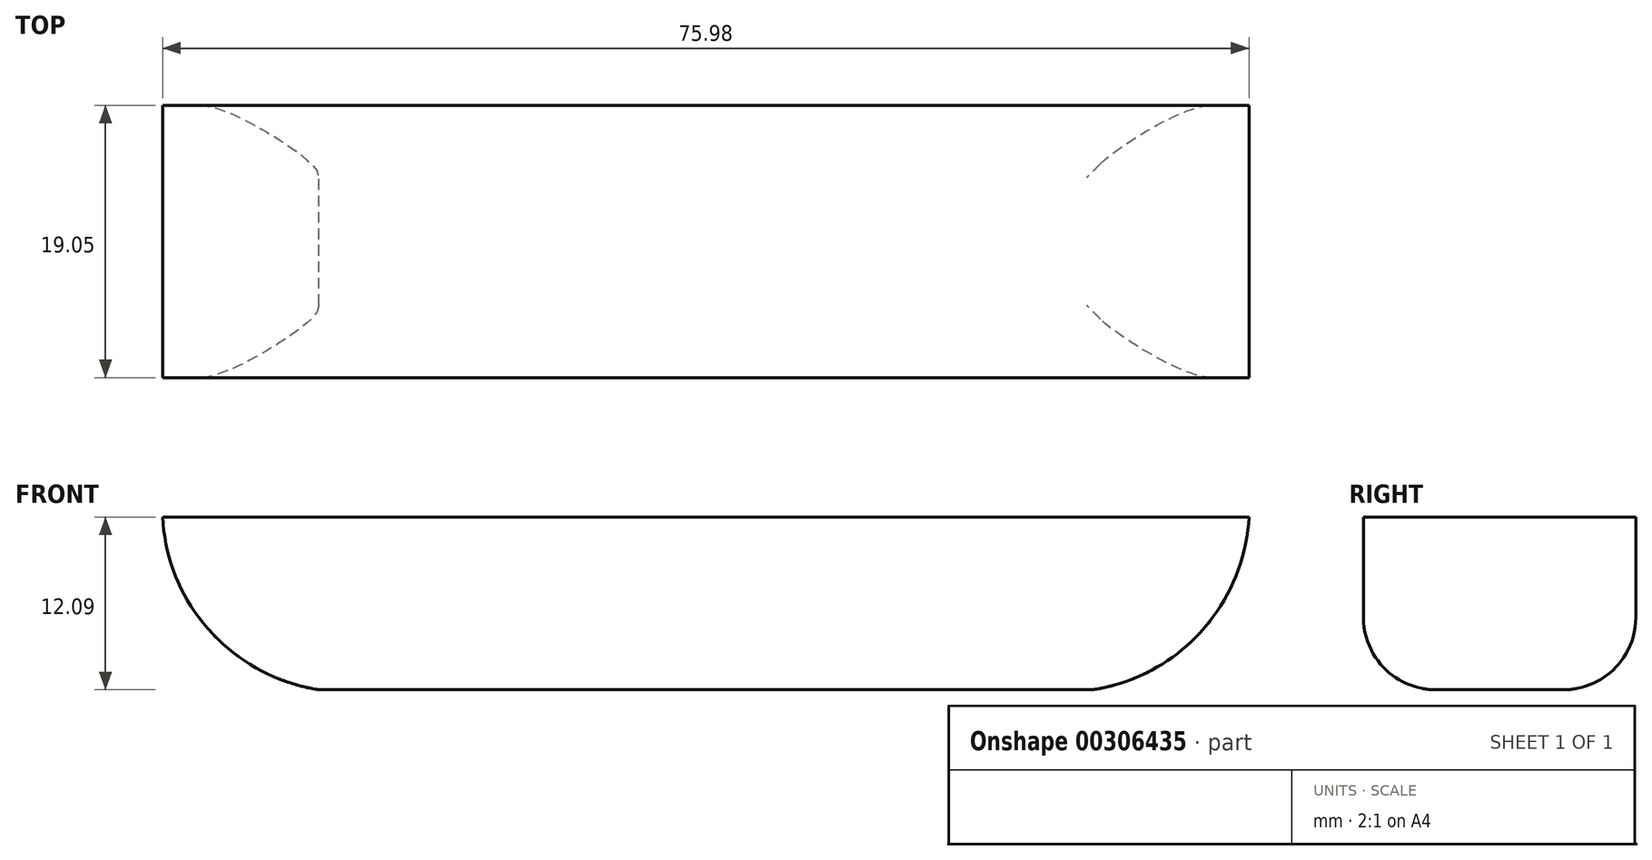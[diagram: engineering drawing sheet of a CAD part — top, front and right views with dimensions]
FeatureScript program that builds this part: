
annotation { "Feature Type Name" : "Feature", "Feature Type Description" : "" }
export const myFeature = defineFeature(function(context is Context, id is Id, definition is map)
    precondition{}
    {
        {
            var Q0;
            Q0=qCreatedBy(makeId("Front.planeOp"),FACE);
            var sketch = newSketch(context, id + "F0", { "sketchPlane" : qUnion([Q0])});
            skLineSegment(sketch, "E0", {"start": v(-51.23, 18.13) * mm, "end": v(24.75, 18.13) * mm});
            skArc(sketch, "E1", {"start": v(13.81, 6.04) * mm, "mid": v(21.43, 10.15) * mm, "end": v(24.75, 18.13) * mm});
            skArc(sketch, "E2.MirrorCS", {"start": v(-40.3, 6.04) * mm, "mid": v(-47.9, 10.15) * mm, "end": v(-51.23, 18.13) * mm});
            skLineSegment(sketch, "E3", {"start": v(-40.3, 6.04) * mm, "end": v(13.81, 6.04) * mm});
            skSolve(sketch);
        }
        {
            var Q0;
            Q0 = qSketchRegion(id + "F0", true);
            extrude(context, id + "F1", {"entities" : qUnion([Q0]), "depth" : 19.05 * mm});
        }
        {
            var Q0;
            Q0=makeQuery(id+"F1.opExtrude","SWEPT_EDGE",EDGE,{"disambiguationData":[OSD([sQuery(id+"F0.wireOp",EDGE,"E1"),sQuery(id+"F0.wireOp",EDGE,"E3")])]});
            var Q1;
            Q1=makeQuery(id+"F1.opExtrude","CAP_EDGE",EDGE,{"disambiguationData":[OSD([sQuery(id+"F0.wireOp",EDGE,"E3")])],"isStart":true});
            var Q2;
            Q2=makeQuery(id+"F1.opExtrude","CAP_EDGE",EDGE,{"disambiguationData":[OSD([sQuery(id+"F0.wireOp",EDGE,"E3")])],"isStart":false});
            fillet(context, id + "F2", {"entities" : qUnion([Q0, Q1, Q2]), "radius" : 5.08 * mm, "tangentPropagation" : true, "allowEdgeOverflow" : false});
        }
    });
